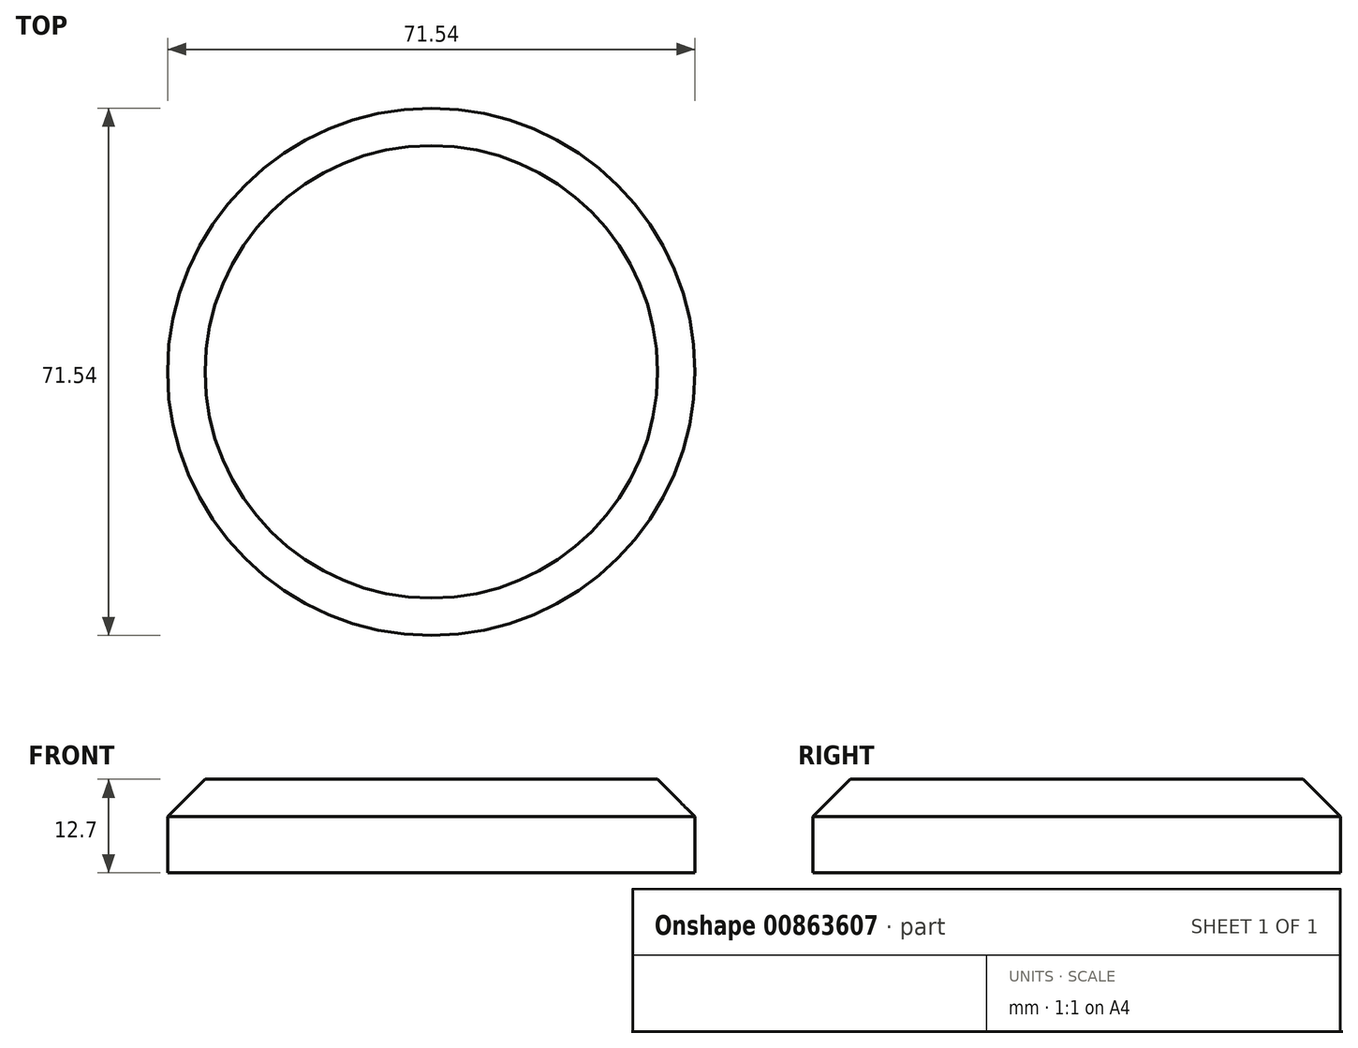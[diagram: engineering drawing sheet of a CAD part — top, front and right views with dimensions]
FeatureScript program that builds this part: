
annotation { "Feature Type Name" : "Feature", "Feature Type Description" : "" }
export const myFeature = defineFeature(function(context is Context, id is Id, definition is map)
    precondition{}
    {
        {
            var Q0;
            Q0=qCreatedBy(makeId("Top.planeOp"),FACE);
            var sketch = newSketch(context, id + "F0", { "sketchPlane" : qUnion([Q0])});
            skCircle(sketch, "E0", {"center": v(0, 0) * mm, "radius": 35.77 * mm});
            skSolve(sketch);
        }
        {
            var Q0;
            Q0=makeQuery(id+"F0.imprint","IMPRINT",FACE,{"disambiguationData":[TD([[makeQuery(id+"F0.imprint","IMPRINT",EDGE,{"derivedFrom":sQuery(id+"F0.wireOp",EDGE,"E0")}),1.0]])]});
            extrude(context, id + "F1", {"entities" : qUnion([Q0]), "depth" : 12.7 * mm, "offsetDistance" : 25.4 * mm});
        }
        {
            var Q0;
            Q0=makeQuery(id+"F1.opExtrude","CAP_FACE",FACE,{"disambiguationData":[OSD([sQuery(id+"F0.wireOp",EDGE,"E0")])],"isStart":false});
            chamfer(context, id + "F2", {"entities" : qUnion([Q0]), "width" : 5.08 * mm, "tangentPropagation" : true});
        }
        {
            var Q0;
            Q0=qCreatedBy(makeId("Front.planeOp"),FACE);
            var sketch = newSketch(context, id + "F3", { "sketchPlane" : qUnion([Q0])});
            skLineSegment(sketch, "E1", {"start": v(-27.28, 0) * mm, "end": v(-13.96, 75.98) * mm});
            skLineSegment(sketch, "E2", {"start": v(-13.96, 75.98) * mm, "end": v(0, 75.98) * mm});
            skLineSegment(sketch, "E3", {"start": v(0, 75.98) * mm, "end": v(0, 73.67) * mm});
            skLineSegment(sketch, "E4", {"start": v(0, 73.67) * mm, "end": v(-11.08, 73.67) * mm});
            skLineSegment(sketch, "E5", {"start": v(-11.08, 73.67) * mm, "end": v(-24, 0) * mm});
            skLineSegment(sketch, "E6", {"start": v(0, 75.98) * mm, "end": v(0, 0) * mm});
            skSolve(sketch);
        }
        {
            var Q0;
            Q0=sQuery(id+"F3.wireOp",EDGE,"E5");
            var Q1;
            Q1=sQuery(id+"F3.wireOp",EDGE,"E1");
            var Q2;
            Q2=sQuery(id+"F3.wireOp",EDGE,"E4");
            var Q3;
            Q3=sQuery(id+"F3.wireOp",EDGE,"E2");
            var Q4;
            Q4=sQuery(id+"F3.wireOp",EDGE,"E6");
            revolve(context, id + "F4", {"bodyType" : ToolBodyType.SURFACE, "surfaceOperationType" : NewSurfaceOperationType.NEW, "surfaceEntities" : qUnion([Q0, Q1, Q2, Q3]), "axis" : qUnion([Q4]), "revolveType" : RevolveType.FULL});
        }
        {
            var Q0;
            Q0=qCreatedBy(makeId("Front.planeOp"),FACE);
            var sketch = newSketch(context, id + "F5", { "sketchPlane" : qUnion([Q0])});
            skLineSegment(sketch, "E7", {"start": v(0, 107.02) * mm, "end": v(0, 75.34) * mm});
            skSolve(sketch);
        }
        {
            var Q0;
            Q0=qCreatedBy(makeId("Front.planeOp"),FACE);
            var sketch = newSketch(context, id + "F6", { "sketchPlane" : qUnion([Q0])});
            skArc(sketch, "E8", {"start": v(0, 75.8) * mm, "mid": v(15.74, 91.48) * mm, "end": v(0, 107.16) * mm});
            skSolve(sketch);
        }
        {
            var Q0;
            Q0=sQuery(id+"F6.wireOp",EDGE,"E8");
            var Q1;
            Q1=sQuery(id+"F5.wireOp",EDGE,"E7");
            revolve(context, id + "F7", {"bodyType" : ToolBodyType.SURFACE, "surfaceOperationType" : NewSurfaceOperationType.NEW, "surfaceEntities" : qUnion([Q0]), "axis" : qUnion([Q1]), "revolveType" : RevolveType.FULL});
        }
    });
